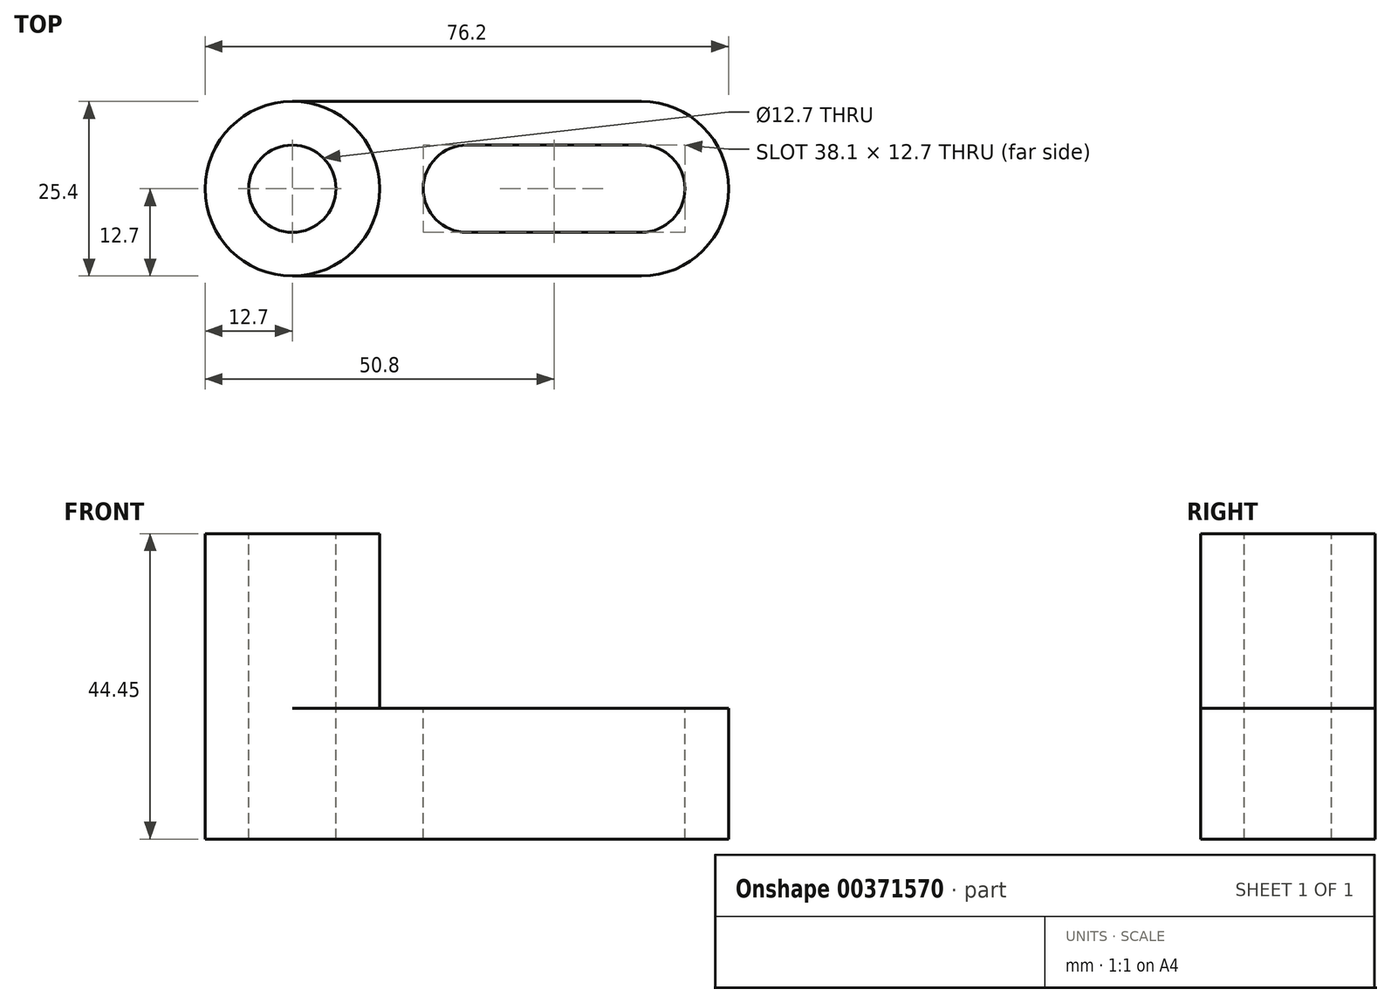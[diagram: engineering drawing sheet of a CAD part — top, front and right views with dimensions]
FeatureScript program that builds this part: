
annotation { "Feature Type Name" : "Feature", "Feature Type Description" : "" }
export const myFeature = defineFeature(function(context is Context, id is Id, definition is map)
    precondition{}
    {
        {
            var Q0;
            Q0=qCreatedBy(makeId("Front.planeOp"),FACE);
            var sketch = newSketch(context, id + "F0", { "sketchPlane" : qUnion([Q0])});
            skLineSegment(sketch, "E0", {"start": v(0, 0) * mm, "end": v(0, 44.45) * mm});
            skLineSegment(sketch, "E1", {"start": v(0, 44.45) * mm, "end": v(25.4, 44.45) * mm});
            skLineSegment(sketch, "E2", {"start": v(25.4, 44.45) * mm, "end": v(25.4, 19.05) * mm});
            skLineSegment(sketch, "E3", {"start": v(25.4, 19.05) * mm, "end": v(76.2, 19.05) * mm});
            skLineSegment(sketch, "E4", {"start": v(76.2, 19.05) * mm, "end": v(76.2, 0) * mm});
            skLineSegment(sketch, "E5", {"start": v(76.2, 0) * mm, "end": v(0, 0) * mm});
            skSolve(sketch);
        }
        {
            var Q0;
            Q0=makeQuery(id+"F0.imprint","IMPRINT",FACE,{"disambiguationData":[TD([[makeQuery(id+"F0.imprint","IMPRINT",EDGE,{"derivedFrom":sQuery(id+"F0.wireOp",EDGE,"E0")}),-1.0]])]});
            extrude(context, id + "F1", {"entities" : qUnion([Q0]), "depth" : 25.4 * mm});
        }
        {
            var Q0;
            Q0=makeQuery(id+"F1.opExtrude","SWEPT_FACE",FACE,{"disambiguationData":[OSD([sQuery(id+"F0.wireOp",EDGE,"E1")])]});
            var sketch = newSketch(context, id + "F2", { "sketchPlane" : qUnion([Q0])});
            skCircle(sketch, "E6", {"center": v(12.7, -12.7) * mm, "radius": 12.7 * mm});
            skPoint(sketch, "E6.centerSnap0", {"position": v(0, -12.7) * mm});
            skCircle(sketch, "E7", {"center": v(12.7, -12.7) * mm, "radius": 6.35 * mm});
            skSolve(sketch);
        }
        {
            var Q0;
            Q0=makeQuery(id+"F2.imprint","IMPRINT",FACE,{"disambiguationData":[TD([[makeQuery(id+"F2.imprint","IMPRINT",EDGE,{"derivedFrom":sQuery(id+"F2.wireOp",EDGE,"E7")}),1.0]])]});
            var Q1;
            {var subQ0=sQuery(id+"F2.wireOp",EDGE,"E6");var subQ1=sQuery(id+"F0.wireOp",EDGE,"E1");var subQ2=makeQuery(id+"F1.opExtrude","CAP_EDGE",EDGE,{"disambiguationData":[OSD([subQ1])],"isStart":true});var subQ3=makeQuery(id+"F2.imprint","INTERSECT",VERTEX,{"derivedFrom":[subQ2,subQ0]});Q1=makeQuery(id+"F2.imprint","IMPRINT",FACE,{"disambiguationData":[TD([[makeQuery(id+"F2.imprint","IMPRINT",EDGE,{"disambiguationData":[TD([[subQ3,-1.0]])],"derivedFrom":subQ0}),-1.0]])]});}
            var Q2;
            {var subQ0=sQuery(id+"F2.wireOp",EDGE,"E6");var subQ1=sQuery(id+"F0.wireOp",EDGE,"E1");var subQ4=makeQuery(id+"F1.opExtrude","CAP_EDGE",EDGE,{"disambiguationData":[OSD([subQ1])],"isStart":false});var subQ5=makeQuery(id+"F2.imprint","INTERSECT",VERTEX,{"derivedFrom":[subQ4,subQ0]});Q2=makeQuery(id+"F2.imprint","IMPRINT",FACE,{"disambiguationData":[TD([[makeQuery(id+"F2.imprint","IMPRINT",EDGE,{"disambiguationData":[TD([[subQ5,1.0]])],"derivedFrom":subQ0}),-1.0]])]});}
            var Q3;
            {var subQ0=sQuery(id+"F2.wireOp",EDGE,"E6");var subQ1=sQuery(id+"F0.wireOp",EDGE,"E1");var subQ4=makeQuery(id+"F1.opExtrude","CAP_EDGE",EDGE,{"disambiguationData":[OSD([subQ1])],"isStart":false});var subQ5=makeQuery(id+"F2.imprint","INTERSECT",VERTEX,{"derivedFrom":[subQ4,subQ0]});Q3=makeQuery(id+"F2.imprint","IMPRINT",FACE,{"disambiguationData":[TD([[makeQuery(id+"F2.imprint","IMPRINT",EDGE,{"disambiguationData":[TD([[subQ5,-1.0]])],"derivedFrom":subQ0}),-1.0]])]});}
            var Q4;
            {var subQ0=sQuery(id+"F2.wireOp",EDGE,"E6");var subQ1=sQuery(id+"F0.wireOp",EDGE,"E1");var subQ2=makeQuery(id+"F1.opExtrude","CAP_EDGE",EDGE,{"disambiguationData":[OSD([subQ1])],"isStart":true});var subQ3=makeQuery(id+"F2.imprint","INTERSECT",VERTEX,{"derivedFrom":[subQ2,subQ0]});Q4=makeQuery(id+"F2.imprint","IMPRINT",FACE,{"disambiguationData":[TD([[makeQuery(id+"F2.imprint","IMPRINT",EDGE,{"disambiguationData":[TD([[subQ3,1.0]])],"derivedFrom":subQ0}),-1.0]])]});}
            extrude(context, id + "F3", {"entities" : qUnion([Q0, Q1, Q2, Q3, Q4]), "operationType" : NewBodyOperationType.REMOVE, "oppositeDirection" : true, "depth" : 25.4 * mm});
        }
        {
            var Q0;
            Q0=makeQuery(id+"F3.boolean.opBoolean","COPY",FACE,{"derivedFrom":makeQuery(id+"F3.opExtrude","CAP_FACE",FACE,{"disambiguationData":[OSD([sQuery(id+"F2.wireOp",EDGE,"E7")])],"isStart":false})});
            extrude(context, id + "F4", {"entities" : qUnion([Q0]), "operationType" : NewBodyOperationType.REMOVE, "oppositeDirection" : true, "depth" : 25.4 * mm});
        }
        {
            var Q0;
            {var subQ0=sQuery(id+"F0.wireOp",EDGE,"E1");var subQ1=makeQuery(id+"F1.opExtrude","CAP_EDGE",EDGE,{"disambiguationData":[OSD([subQ0])],"isStart":true});var subQ2=sQuery(id+"F0.wireOp",EDGE,"E0");var subQ3=makeQuery(id+"F1.opExtrude","SWEPT_EDGE",EDGE,{"disambiguationData":[OSD([subQ2,subQ0])]});var subQ4=makeQuery(id+"F2.imprint","INTERSECT",VERTEX,{"derivedFrom":[subQ3,subQ1]});var subQ5=sQuery(id+"F2.wireOp",EDGE,"E6");var subQ6=makeQuery(id+"F2.imprint","INTERSECT",VERTEX,{"derivedFrom":[subQ1,subQ5]});Q0=makeQuery(id+"F3.boolean.opBoolean","COPY",FACE,{"derivedFrom":makeQuery(id+"F3.opExtrude","CAP_FACE",FACE,{"disambiguationData":[OSD([subQ2,subQ0,subQ5]),TDD([makeQuery(id+"F2.imprint","IMPRINT",EDGE,{"disambiguationData":[TD([[subQ6,-1.0]])],"derivedFrom":subQ5}),makeQuery(id+"F2.imprint","IMPRINT",EDGE,{"disambiguationData":[TD([[subQ4,1.0]])],"derivedFrom":subQ3}),makeQuery(id+"F2.imprint","IMPRINT",EDGE,{"disambiguationData":[TD([[subQ6,1.0]])],"derivedFrom":subQ1})])],"isStart":false})});}
            var Q1;
            {var subQ0=sQuery(id+"F0.wireOp",EDGE,"E1");var subQ1=makeQuery(id+"F1.opExtrude","CAP_EDGE",EDGE,{"disambiguationData":[OSD([subQ0])],"isStart":false});var subQ2=sQuery(id+"F0.wireOp",EDGE,"E0");var subQ3=makeQuery(id+"F1.opExtrude","SWEPT_EDGE",EDGE,{"disambiguationData":[OSD([subQ2,subQ0])]});var subQ4=makeQuery(id+"F2.imprint","INTERSECT",VERTEX,{"derivedFrom":[subQ3,subQ1]});var subQ5=sQuery(id+"F2.wireOp",EDGE,"E6");var subQ6=makeQuery(id+"F2.imprint","INTERSECT",VERTEX,{"derivedFrom":[subQ1,subQ5]});Q1=makeQuery(id+"F3.boolean.opBoolean","COPY",FACE,{"derivedFrom":makeQuery(id+"F3.opExtrude","CAP_FACE",FACE,{"disambiguationData":[OSD([subQ2,subQ0,subQ5]),TDD([makeQuery(id+"F2.imprint","IMPRINT",EDGE,{"disambiguationData":[TD([[subQ6,1.0]])],"derivedFrom":subQ5}),makeQuery(id+"F2.imprint","IMPRINT",EDGE,{"disambiguationData":[TD([[subQ4,-1.0]])],"derivedFrom":subQ3}),makeQuery(id+"F2.imprint","IMPRINT",EDGE,{"disambiguationData":[TD([[subQ6,1.0]])],"derivedFrom":subQ1})])],"isStart":false})});}
            extrude(context, id + "F5", {"entities" : qUnion([Q0, Q1]), "operationType" : NewBodyOperationType.REMOVE, "oppositeDirection" : true, "depth" : 25.4 * mm});
        }
        {
            var Q0;
            {var subQ0=sQuery(id+"F0.wireOp",EDGE,"E1");var subQ1=makeQuery(id+"F1.opExtrude","CAP_EDGE",EDGE,{"disambiguationData":[OSD([subQ0])],"isStart":false});var subQ2=sQuery(id+"F0.wireOp",EDGE,"E2");var subQ3=makeQuery(id+"F1.opExtrude","SWEPT_EDGE",EDGE,{"disambiguationData":[OSD([subQ0,subQ2])]});var subQ4=makeQuery(id+"F2.imprint","INTERSECT",VERTEX,{"derivedFrom":[subQ3,subQ1]});var subQ5=sQuery(id+"F2.wireOp",EDGE,"E6");var subQ6=makeQuery(id+"F2.imprint","INTERSECT",VERTEX,{"derivedFrom":[subQ1,subQ5]});var subQ8=makeQuery(id+"F1.opExtrude","CAP_EDGE",EDGE,{"disambiguationData":[OSD([subQ0])],"isStart":true});var subQ9=makeQuery(id+"F2.imprint","INTERSECT",VERTEX,{"derivedFrom":[subQ3,subQ8]});var subQ10=makeQuery(id+"F2.imprint","INTERSECT",VERTEX,{"derivedFrom":[subQ8,subQ5]});Q0=makeQuery(id+"F3.boolean.opBoolean","MERGE",FACE,{"derivedFrom":[makeQuery(id+"F1.opExtrude","SWEPT_FACE",FACE,{"disambiguationData":[OSD([sQuery(id+"F0.wireOp",EDGE,"E3")])]}),makeQuery(id+"F3.opExtrude","CAP_FACE",FACE,{"disambiguationData":[OSD([subQ0,subQ2,subQ5]),TDD([makeQuery(id+"F2.imprint","IMPRINT",EDGE,{"disambiguationData":[TD([[subQ10,1.0]])],"derivedFrom":subQ5}),makeQuery(id+"F2.imprint","IMPRINT",EDGE,{"disambiguationData":[TD([[subQ9,1.0]])],"derivedFrom":subQ3}),makeQuery(id+"F2.imprint","IMPRINT",EDGE,{"disambiguationData":[TD([[subQ10,-1.0]])],"derivedFrom":subQ8})])],"isStart":false}),makeQuery(id+"F3.opExtrude","CAP_FACE",FACE,{"disambiguationData":[OSD([subQ0,subQ2,subQ5]),TDD([makeQuery(id+"F2.imprint","IMPRINT",EDGE,{"disambiguationData":[TD([[subQ6,-1.0]])],"derivedFrom":subQ5}),makeQuery(id+"F2.imprint","IMPRINT",EDGE,{"disambiguationData":[TD([[subQ4,-1.0]])],"derivedFrom":subQ3}),makeQuery(id+"F2.imprint","IMPRINT",EDGE,{"disambiguationData":[TD([[subQ6,-1.0]])],"derivedFrom":subQ1})])],"isStart":false})]});}
            var sketch = newSketch(context, id + "F6", { "sketchPlane" : qUnion([Q0])});
            skArc(sketch, "E8", {"start": v(63.5, -25.4) * mm, "mid": v(76.2, -12.7) * mm, "end": v(63.5, 0) * mm});
            skCircle(sketch, "E9", {"center": v(63.5, -12.7) * mm, "radius": 6.35 * mm});
            skCircle(sketch, "E10", {"center": v(38.1, -12.7) * mm, "radius": 6.35 * mm});
            skLineSegment(sketch, "E11", {"start": v(38.1, -6.35) * mm, "end": v(63.5, -6.35) * mm});
            skLineSegment(sketch, "E12", {"start": v(38.1, -19.05) * mm, "end": v(63.5, -19.05) * mm});
            skSolve(sketch);
        }
        {
            var Q0;
            {var subQ0=sQuery(id+"F6.wireOp",EDGE,"E10");var subQ1=makeQuery(id+"F6.imprint","INTERSECT",VERTEX,{"derivedFrom":[subQ0,sQuery(id+"F6.wireOp",EDGE,"E11")]});Q0=makeQuery(id+"F6.imprint","IMPRINT",FACE,{"disambiguationData":[TD([[makeQuery(id+"F6.imprint","IMPRINT",EDGE,{"disambiguationData":[TD([[subQ1,-1.0]])],"derivedFrom":subQ0}),1.0]])]});}
            var Q1;
            {var subQ0=sQuery(id+"F6.wireOp",EDGE,"E11");Q1=makeQuery(id+"F6.imprint","IMPRINT",FACE,{"disambiguationData":[TD([[makeQuery(id+"F6.imprint","IMPRINT",EDGE,{"derivedFrom":subQ0}),-1.0]])]});}
            var Q2;
            {var subQ0=sQuery(id+"F6.wireOp",EDGE,"E9");var subQ1=makeQuery(id+"F6.imprint","INTERSECT",VERTEX,{"derivedFrom":[subQ0,sQuery(id+"F6.wireOp",EDGE,"E11")]});Q2=makeQuery(id+"F6.imprint","IMPRINT",FACE,{"disambiguationData":[TD([[makeQuery(id+"F6.imprint","IMPRINT",EDGE,{"disambiguationData":[TD([[subQ1,-1.0]])],"derivedFrom":subQ0}),1.0]])]});}
            var Q3;
            {var subQ0=sQuery(id+"F6.wireOp",EDGE,"E8");var subQ1=sQuery(id+"F0.wireOp",EDGE,"E3");var subQ2=makeQuery(id+"F1.opExtrude","SWEPT_EDGE",EDGE,{"disambiguationData":[OSD([subQ1,sQuery(id+"F0.wireOp",EDGE,"E4")])]});var subQ3=makeQuery(id+"F6.imprint","INTERSECT",VERTEX,{"derivedFrom":[subQ2,subQ0]});Q3=makeQuery(id+"F6.imprint","IMPRINT",FACE,{"disambiguationData":[TD([[makeQuery(id+"F6.imprint","IMPRINT",EDGE,{"disambiguationData":[TD([[subQ3,-1.0]])],"derivedFrom":subQ0}),-1.0]])]});}
            var Q4;
            {var subQ0=sQuery(id+"F6.wireOp",EDGE,"E8");var subQ1=sQuery(id+"F0.wireOp",EDGE,"E3");var subQ2=makeQuery(id+"F1.opExtrude","SWEPT_EDGE",EDGE,{"disambiguationData":[OSD([subQ1,sQuery(id+"F0.wireOp",EDGE,"E4")])]});var subQ3=makeQuery(id+"F6.imprint","INTERSECT",VERTEX,{"derivedFrom":[subQ2,subQ0]});Q4=makeQuery(id+"F6.imprint","IMPRINT",FACE,{"disambiguationData":[TD([[makeQuery(id+"F6.imprint","IMPRINT",EDGE,{"disambiguationData":[TD([[subQ3,1.0]])],"derivedFrom":subQ0}),-1.0]])]});}
            extrude(context, id + "F7", {"entities" : qUnion([Q0, Q1, Q2, Q3, Q4]), "operationType" : NewBodyOperationType.REMOVE, "oppositeDirection" : true, "depth" : 25.4 * mm});
        }
    });
